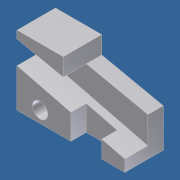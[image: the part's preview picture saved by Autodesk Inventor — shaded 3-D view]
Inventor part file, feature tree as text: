
AUTODESK INVENTOR PART (.ipt)
format: ipt  version: unknown  size: 206,848 bytes
history: native  units: in
note: dims shown in document units (in); Inventor stores cm internally (conversion verified against a paired STEP export)
features: sketch x5, extrude x4, hole x1
ambient origin geometry x8: Origin, YZ Plane, XZ Plane, XY Plane, X Axis, Y Axis, Z Axis, Center Point
bodies: Solid1 (feature_tree)
feature tree (10):
  extrude  "Extrusion1"  Depth=4.5in
  extrude  "Extrusion2"  Depth=2.5in
  extrude  "Extrusion3"  Depth=0.5in
  sketch  "Sketch5"  dims[d7=2.0in d8=1.5in d9=0.0in]
  extrude  "Extrusion4"  Depth=1.5in TaperAngle=0.0deg
  hole  "Hole1"  [1 undecoded]
  sketch  "Sketch1"  dims[d0=7.0in d1=4.5in]
  sketch  "Sketch2"  dims[d2=2.5in d3=0.0in d4=2.5in]
  sketch  "Sketch4"  dims[d5=0.75in d6=0.5in]
  sketch  "Sketch7"  dims[d11=2.0in d12=1.0in d13=0.0in d14=3.0in d15=3.0in d16=4.0in d22=1.0in d23=0.0in d24=1.5in d25=0.75in d26=1.0in d27=0.75in d28=0.375in d29=0.25in d30=0.5635in d31=1.0in d32=0.8108in]
note: 1 required parameter value undecoded (feature->parameter linkage not recoverable at this tier; creation-order binding heuristic only, values carry confidence <= 0.55)
